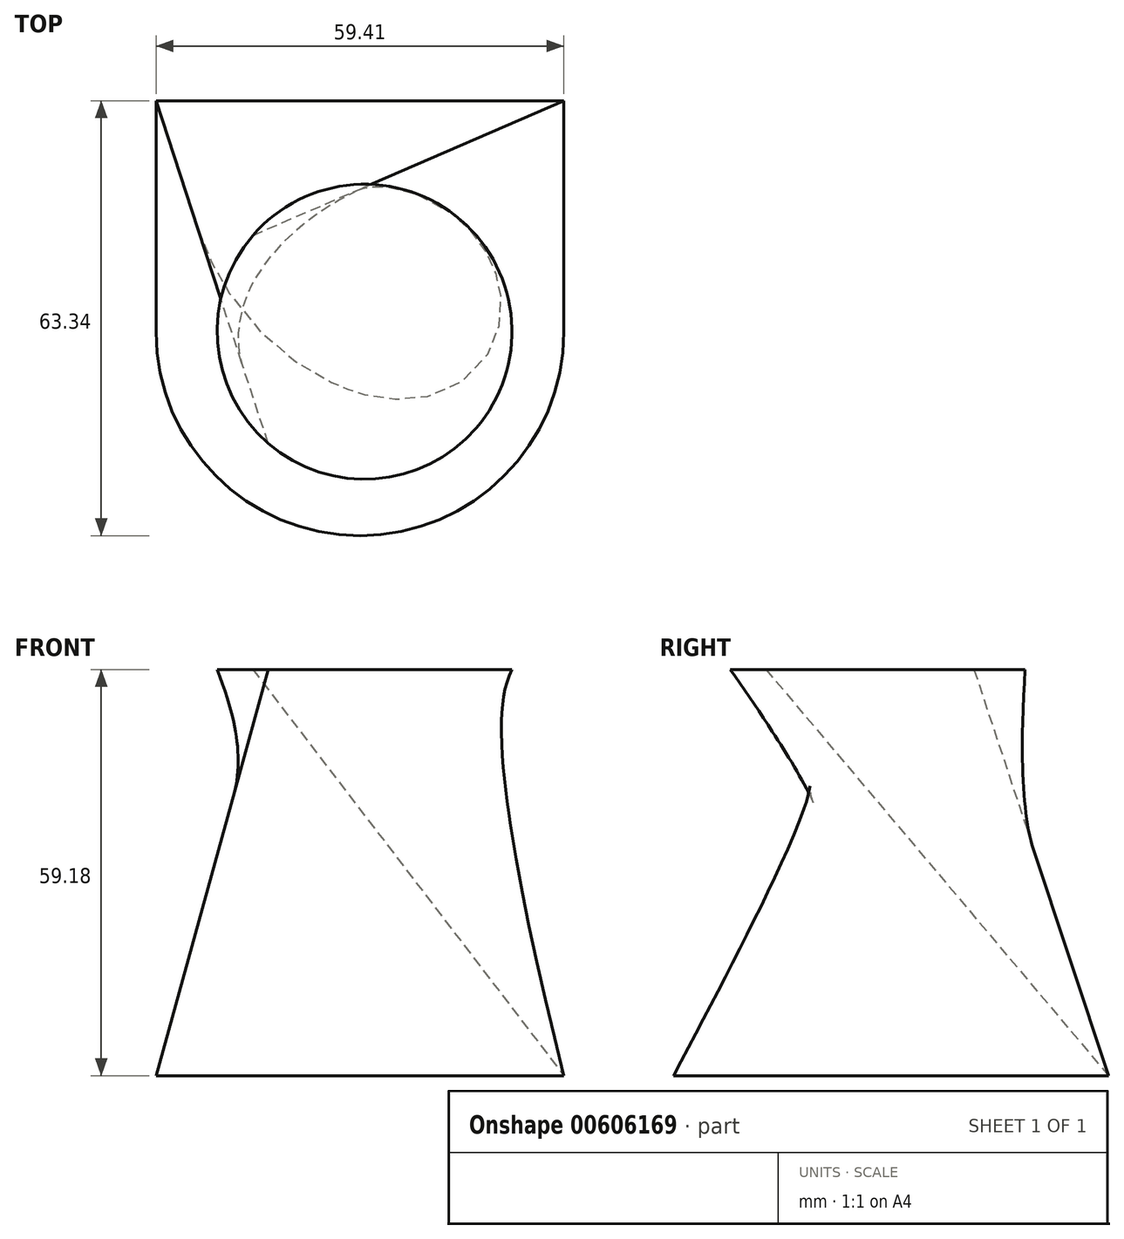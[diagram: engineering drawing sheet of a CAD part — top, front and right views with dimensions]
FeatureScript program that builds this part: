
annotation { "Feature Type Name" : "Feature", "Feature Type Description" : "" }
export const myFeature = defineFeature(function(context is Context, id is Id, definition is map)
    precondition{}
    {
        {
            var Q0;
            Q0=qCreatedBy(makeId("Top.planeOp"),FACE);
            var sketch = newSketch(context, id + "F0", { "sketchPlane" : qUnion([Q0])});
            skLineSegment(sketch, "E0.top", {"start": v(59.41, 33.63) * mm, "end": v(0, 33.63) * mm});
            skLineSegment(sketch, "E0.left", {"start": v(0, 0) * mm, "end": v(0, 33.63) * mm});
            skLineSegment(sketch, "E0.right", {"start": v(59.41, 0) * mm, "end": v(59.41, 33.63) * mm});
            skArc(sketch, "E1", {"start": v(0, 0) * mm, "mid": v(29.7, -29.7) * mm, "end": v(59.41, 0) * mm});
            skSolve(sketch);
        }
        {
            var Q0;
            Q0=qCreatedBy(makeId("Top.planeOp"),FACE);
            cPlane(context, id + "F1", {"entities" : qUnion([Q0]), "cplaneType" : CPlaneType.OFFSET, "offset" : 59.18 * mm, "width" : 152.4 * mm, "height" : 152.4 * mm});
        }
        {
            var Q0;
            Q0=qCreatedBy(id+"F1.planeOp",FACE);
            var sketch = newSketch(context, id + "F2", { "sketchPlane" : qUnion([Q0])});
            skCircle(sketch, "E2", {"center": v(30.37, 0) * mm, "radius": 21.48 * mm});
            skSolve(sketch);
        }
        {
            var Q0;
            Q0 = qSketchRegion(id + "F2", true);
            var Q1;
            Q1 = qSketchRegion(id + "F0", true);
            loft(context, id + "F3", {"sheetProfilesArray" : [{ "sheetProfileEntities" : qUnion([Q0]) }, { "sheetProfileEntities" : qUnion([Q1]) }]});
        }
    });
